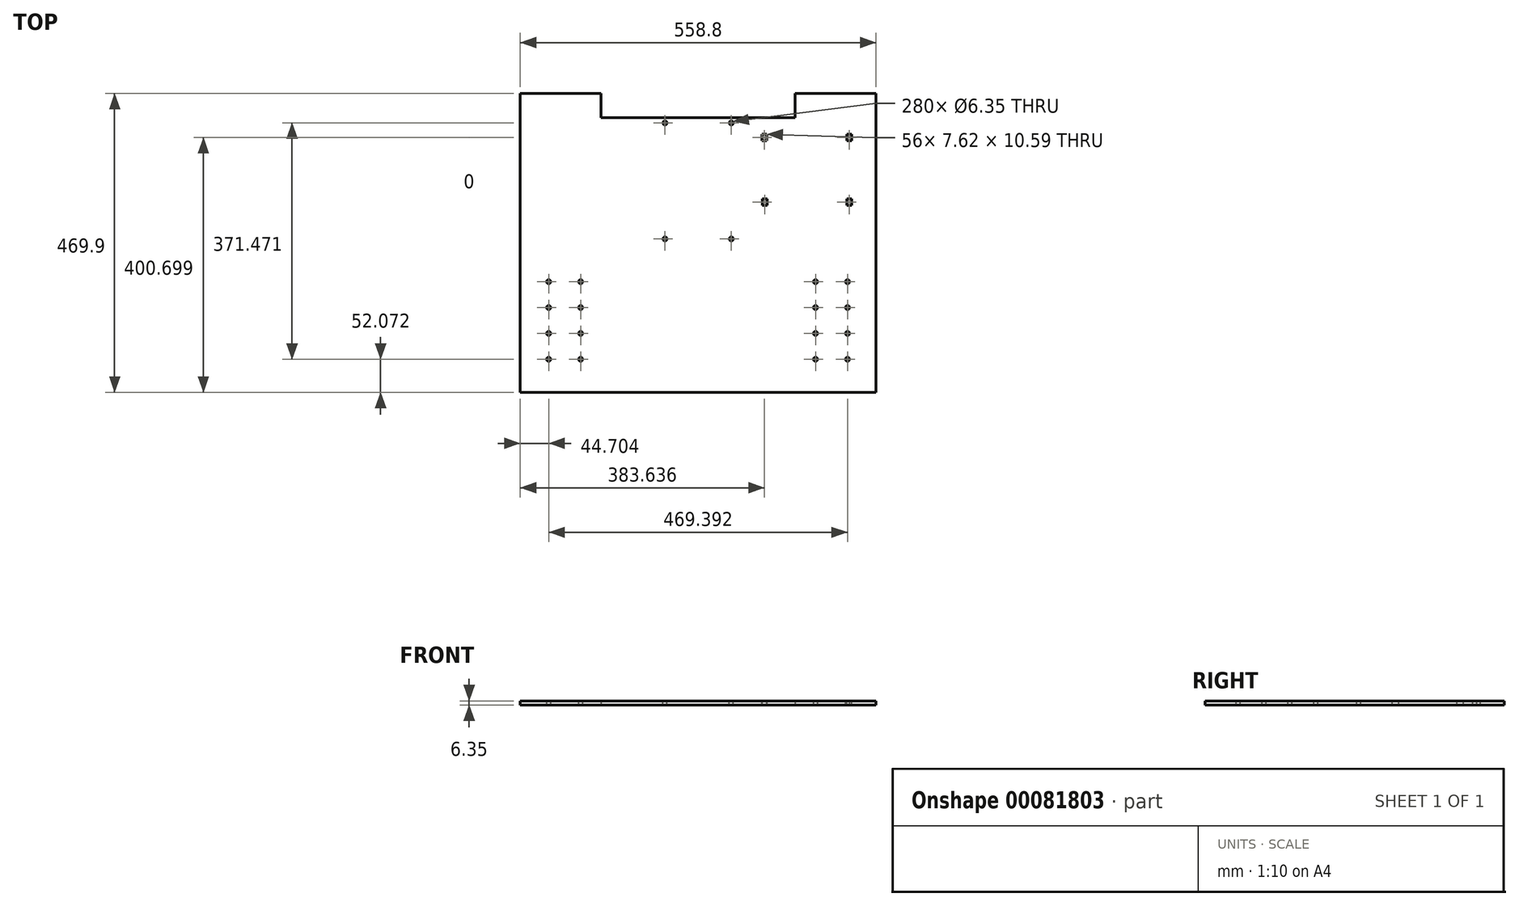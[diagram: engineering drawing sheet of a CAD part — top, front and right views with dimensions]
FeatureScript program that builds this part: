
annotation { "Feature Type Name" : "Feature", "Feature Type Description" : "" }
export const myFeature = defineFeature(function(context is Context, id is Id, definition is map)
    precondition{}
    {
        {
            var Q0;
            Q0=qCreatedBy(makeId("Top.planeOp"),FACE);
            var sketch = newSketch(context, id + "F0", { "sketchPlane" : qUnion([Q0])});
            skLineSegment(sketch, "E0.top", {"start": v(-279.4, -241.27) * mm, "end": v(279.4, -241.27) * mm});
            skLineSegment(sketch, "E0.left", {"start": v(-279.4, 228.63) * mm, "end": v(-279.4, -241.27) * mm});
            skLineSegment(sketch, "E0.right", {"start": v(279.4, 228.63) * mm, "end": v(279.4, -241.27) * mm});
            skLineSegment(sketch, "E1.top", {"start": v(-152.4, 190.53) * mm, "end": v(152.4, 190.53) * mm});
            skLineSegment(sketch, "E1.left", {"start": v(-152.4, 228.63) * mm, "end": v(-152.4, 190.53) * mm});
            skLineSegment(sketch, "E1.right", {"start": v(152.4, 228.63) * mm, "end": v(152.4, 190.53) * mm});
            skLineSegment(sketch, "E2", {"start": v(-279.4, 228.63) * mm, "end": v(-152.4, 228.63) * mm});
            skLineSegment(sketch, "E3", {"start": v(152.4, 228.63) * mm, "end": v(279.4, 228.63) * mm});
            skSolve(sketch);
        }
        {
            var Q0;
            Q0=makeQuery(id+"F0.imprint","IMPRINT",FACE,{"disambiguationData":[TD([[makeQuery(id+"F0.imprint","IMPRINT",EDGE,{"derivedFrom":sQuery(id+"F0.wireOp",EDGE,"E0.top")}),1.0]])]});
            extrude(context, id + "F1", {"entities" : qUnion([Q0]), "depth" : 6.35 * mm});
        }
        {
            var Q0;
            Q0=makeQuery(id+"F1.opExtrude","CAP_FACE",FACE,{"disambiguationData":[OSD([sQuery(id+"F0.wireOp",EDGE,"E0.top"),sQuery(id+"F0.wireOp",EDGE,"E0.left"),sQuery(id+"F0.wireOp",EDGE,"E0.right"),sQuery(id+"F0.wireOp",EDGE,"E1.top"),sQuery(id+"F0.wireOp",EDGE,"E1.left"),sQuery(id+"F0.wireOp",EDGE,"E1.right"),sQuery(id+"F0.wireOp",EDGE,"E2"),sQuery(id+"F0.wireOp",EDGE,"E3")])],"isStart":false});
            var sketch = newSketch(context, id + "F2", { "sketchPlane" : qUnion([Q0])});
            skLineSegment(sketch, "E4.bottom", {"start": v(-241.3, -203.17) * mm, "end": v(-177.8, -203.17) * mm});
            skLineSegment(sketch, "E4.top", {"start": v(-241.3, -175.23) * mm, "end": v(-177.8, -175.23) * mm});
            skLineSegment(sketch, "E4.left", {"start": v(-241.3, -203.17) * mm, "end": v(-241.3, -175.23) * mm});
            skLineSegment(sketch, "E4.right", {"start": v(-177.8, -203.17) * mm, "end": v(-177.8, -175.23) * mm});
            skCircle(sketch, "E5", {"center": v(-234.69, -189.2) * mm, "radius": 2.2 * mm});
            skCircle(sketch, "E6", {"center": v(-184.42, -189.2) * mm, "radius": 2.2 * mm});
            skSolve(sketch);
        }
        {
            var Q0;
            Q0=sQuery(id+"F2.wireOp",VERTEX,"E5.center");
            var Q1;
            Q1=sQuery(id+"F2.wireOp",VERTEX,"E6.center");
            var Q2;
            Q2=makeQuery(id+"F1.opExtrude","SWEPT_BODY",BODY,{"disambiguationData":[OSD([sQuery(id+"F0.wireOp",EDGE,"E0.top"),sQuery(id+"F0.wireOp",EDGE,"E0.left"),sQuery(id+"F0.wireOp",EDGE,"E0.right"),sQuery(id+"F0.wireOp",EDGE,"E1.top"),sQuery(id+"F0.wireOp",EDGE,"E1.left"),sQuery(id+"F0.wireOp",EDGE,"E1.right"),sQuery(id+"F0.wireOp",EDGE,"E2"),sQuery(id+"F0.wireOp",EDGE,"E3")])]});
            hole(context, id + "F3", {"style" : HoleStyle.SIMPLE, "endStyle" : HoleEndStyle.THROUGH, "holeDiameter" : 6.35 * mm, "locations" : qUnion([Q0, Q1]), "scope" : qUnion([Q2]), "isTappedThrough" : true});
        }
        {
            var Q0;
            Q0=makeQuery(id+"F2.imprint","IMPRINT",FACE,{"disambiguationData":[TD([[makeQuery(id+"F2.imprint","IMPRINT",EDGE,{"derivedFrom":sQuery(id+"F2.wireOp",EDGE,"E4.bottom")}),-1.0]])]});
            var sketch = newSketch(context, id + "F4", { "sketchPlane" : qUnion([Q0])});
            skCircle(sketch, "E7", {"center": v(-234.7, -148.56) * mm, "radius": 3.18 * mm});
            skCircle(sketch, "E8", {"center": v(-234.7, -107.92) * mm, "radius": 3.18 * mm});
            skCircle(sketch, "E9", {"center": v(-234.7, -67.28) * mm, "radius": 3.18 * mm});
            skLineSegment(sketch, "E10", {"start": v(-241.3, -175.23) * mm, "end": v(-98.93, -175.23) * mm});
            skCircle(sketch, "E11", {"center": v(-184.43, -67.28) * mm, "radius": 3.18 * mm});
            skCircle(sketch, "E12", {"center": v(-184.43, -107.92) * mm, "radius": 3.18 * mm});
            skCircle(sketch, "E13", {"center": v(-184.43, -148.56) * mm, "radius": 3.18 * mm});
            skSolve(sketch);
        }
        {
            var Q0;
            Q0=sQuery(id+"F4.wireOp",VERTEX,"E9.center");
            var Q1;
            Q1=sQuery(id+"F4.wireOp",VERTEX,"E11.center");
            var Q2;
            Q2=sQuery(id+"F4.wireOp",VERTEX,"E12.center");
            var Q3;
            Q3=sQuery(id+"F4.wireOp",VERTEX,"E8.center");
            var Q4;
            Q4=sQuery(id+"F4.wireOp",VERTEX,"E7.center");
            var Q5;
            Q5=sQuery(id+"F4.wireOp",VERTEX,"E13.center");
            var Q6;
            Q6=makeQuery(id+"F1.opExtrude","SWEPT_BODY",BODY,{"disambiguationData":[OSD([sQuery(id+"F0.wireOp",EDGE,"E0.top"),sQuery(id+"F0.wireOp",EDGE,"E0.left"),sQuery(id+"F0.wireOp",EDGE,"E0.right"),sQuery(id+"F0.wireOp",EDGE,"E1.top"),sQuery(id+"F0.wireOp",EDGE,"E1.left"),sQuery(id+"F0.wireOp",EDGE,"E1.right"),sQuery(id+"F0.wireOp",EDGE,"E2"),sQuery(id+"F0.wireOp",EDGE,"E3")])]});
            hole(context, id + "F5", {"style" : HoleStyle.SIMPLE, "endStyle" : HoleEndStyle.THROUGH, "holeDiameter" : 6.35 * mm, "locations" : qUnion([Q0, Q1, Q2, Q3, Q4, Q5]), "scope" : qUnion([Q6]), "isTappedThrough" : true});
        }
        {
            var Q0;
            Q0=makeQuery(id+"F2.imprint","IMPRINT",FACE,{"disambiguationData":[TD([[makeQuery(id+"F2.imprint","IMPRINT",EDGE,{"derivedFrom":sQuery(id+"F2.wireOp",EDGE,"E4.bottom")}),-1.0]])]});
            var sketch = newSketch(context, id + "F6", { "sketchPlane" : qUnion([Q0])});
            skLineSegment(sketch, "E14.bottom", {"start": v(177.8, -203.17) * mm, "end": v(241.3, -203.17) * mm});
            skLineSegment(sketch, "E14.top", {"start": v(177.8, -175.23) * mm, "end": v(241.3, -175.23) * mm});
            skLineSegment(sketch, "E14.left", {"start": v(177.8, -203.17) * mm, "end": v(177.8, -175.23) * mm});
            skLineSegment(sketch, "E14.right", {"start": v(241.3, -203.17) * mm, "end": v(241.3, -175.23) * mm});
            skCircle(sketch, "E15", {"center": v(184.4, -189.2) * mm, "radius": 3.18 * mm});
            skCircle(sketch, "E16", {"center": v(234.67, -189.2) * mm, "radius": 3.18 * mm});
            skSolve(sketch);
        }
        {
            var Q0;
            Q0=makeQuery(id+"F2.imprint","IMPRINT",FACE,{"disambiguationData":[TD([[makeQuery(id+"F2.imprint","IMPRINT",EDGE,{"derivedFrom":sQuery(id+"F2.wireOp",EDGE,"E4.bottom")}),-1.0]])]});
            var sketch = newSketch(context, id + "F7", { "sketchPlane" : qUnion([Q0])});
            skCircle(sketch, "E17", {"center": v(184.43, -148.56) * mm, "radius": 3.18 * mm});
            skCircle(sketch, "E18", {"center": v(234.7, -148.56) * mm, "radius": 3.18 * mm});
            skLineSegment(sketch, "E19", {"start": v(241.7, -175.23) * mm, "end": v(151.62, -175.23) * mm});
            skCircle(sketch, "E20", {"center": v(234.7, -107.92) * mm, "radius": 3.17 * mm});
            skCircle(sketch, "E21", {"center": v(184.43, -107.92) * mm, "radius": 3.18 * mm});
            skCircle(sketch, "E22", {"center": v(184.43, -67.28) * mm, "radius": 3.18 * mm});
            skCircle(sketch, "E23", {"center": v(234.7, -67.28) * mm, "radius": 3.18 * mm});
            skSolve(sketch);
        }
        {
            var Q0;
            Q0=sQuery(id+"F6.wireOp",VERTEX,"E15.center");
            var Q1;
            Q1=sQuery(id+"F6.wireOp",VERTEX,"E16.center");
            var Q2;
            Q2=sQuery(id+"F7.wireOp",VERTEX,"E18.center");
            var Q3;
            Q3=sQuery(id+"F7.wireOp",VERTEX,"E17.center");
            var Q4;
            Q4=sQuery(id+"F7.wireOp",VERTEX,"E21.center");
            var Q5;
            Q5=sQuery(id+"F7.wireOp",VERTEX,"E20.center");
            var Q6;
            Q6=sQuery(id+"F7.wireOp",VERTEX,"E23.center");
            var Q7;
            Q7=sQuery(id+"F7.wireOp",VERTEX,"E22.center");
            var Q8;
            Q8=makeQuery(id+"F1.opExtrude","SWEPT_BODY",BODY,{"disambiguationData":[OSD([sQuery(id+"F0.wireOp",EDGE,"E0.top"),sQuery(id+"F0.wireOp",EDGE,"E0.left"),sQuery(id+"F0.wireOp",EDGE,"E0.right"),sQuery(id+"F0.wireOp",EDGE,"E1.top"),sQuery(id+"F0.wireOp",EDGE,"E1.left"),sQuery(id+"F0.wireOp",EDGE,"E1.right"),sQuery(id+"F0.wireOp",EDGE,"E2"),sQuery(id+"F0.wireOp",EDGE,"E3")])]});
            hole(context, id + "F8", {"style" : HoleStyle.SIMPLE, "endStyle" : HoleEndStyle.THROUGH, "holeDiameter" : 6.35 * mm, "locations" : qUnion([Q0, Q1, Q2, Q3, Q4, Q5, Q6, Q7]), "scope" : qUnion([Q8]), "isTappedThrough" : true});
        }
        {
            var Q0;
            Q0=makeQuery(id+"F2.imprint","IMPRINT",FACE,{"disambiguationData":[TD([[makeQuery(id+"F2.imprint","IMPRINT",EDGE,{"derivedFrom":sQuery(id+"F2.wireOp",EDGE,"E4.bottom")}),-1.0]])]});
            var sketch = newSketch(context, id + "F9", { "sketchPlane" : qUnion([Q0])});
            skLineSegment(sketch, "E24.top", {"start": v(-57.15, -14.11) * mm, "end": v(57.15, -14.11) * mm});
            skLineSegment(sketch, "E24.left", {"start": v(-57.15, 177.83) * mm, "end": v(-57.15, -14.11) * mm});
            skLineSegment(sketch, "E24.right", {"start": v(57.15, 177.83) * mm, "end": v(57.15, -14.11) * mm});
            skCircle(sketch, "E25", {"center": v(-52.07, 182.27) * mm, "radius": 2.67 * mm});
            skCircle(sketch, "E26", {"center": v(52.07, 182.27) * mm, "radius": 2.67 * mm});
            skCircle(sketch, "E27", {"center": v(-52.07, 0) * mm, "radius": 2.67 * mm});
            skCircle(sketch, "E28", {"center": v(52.07, 0) * mm, "radius": 2.67 * mm});
            skSolve(sketch);
        }
        {
            var Q0;
            Q0=sQuery(id+"F9.wireOp",VERTEX,"E25.center");
            var Q1;
            Q1=sQuery(id+"F9.wireOp",VERTEX,"E26.center");
            var Q2;
            Q2=sQuery(id+"F9.wireOp",VERTEX,"E28.center");
            var Q3;
            Q3=sQuery(id+"F9.wireOp",VERTEX,"E27.center");
            var Q4;
            Q4=makeQuery(id+"F1.opExtrude","SWEPT_BODY",BODY,{"disambiguationData":[OSD([sQuery(id+"F0.wireOp",EDGE,"E0.top"),sQuery(id+"F0.wireOp",EDGE,"E0.left"),sQuery(id+"F0.wireOp",EDGE,"E0.right"),sQuery(id+"F0.wireOp",EDGE,"E1.top"),sQuery(id+"F0.wireOp",EDGE,"E1.left"),sQuery(id+"F0.wireOp",EDGE,"E1.right"),sQuery(id+"F0.wireOp",EDGE,"E2"),sQuery(id+"F0.wireOp",EDGE,"E3")])]});
            hole(context, id + "F10", {"style" : HoleStyle.SIMPLE, "endStyle" : HoleEndStyle.THROUGH, "holeDiameter" : 6.35 * mm, "locations" : qUnion([Q0, Q1, Q2, Q3]), "scope" : qUnion([Q4]), "isTappedThrough" : true});
        }
        {
            var Q0;
            Q0=makeQuery(id+"F2.imprint","IMPRINT",FACE,{"disambiguationData":[TD([[makeQuery(id+"F2.imprint","IMPRINT",EDGE,{"derivedFrom":sQuery(id+"F2.wireOp",EDGE,"E4.bottom")}),-1.0]])]});
            var sketch = newSketch(context, id + "F11", { "sketchPlane" : qUnion([Q0])});
            skLineSegment(sketch, "E29.bottom", {"start": v(100.36, 177.83) * mm, "end": v(241.3, 177.83) * mm});
            skLineSegment(sketch, "E29.top", {"start": v(100.36, 39.43) * mm, "end": v(241.3, 39.43) * mm});
            skLineSegment(sketch, "E29.left", {"start": v(100.36, 177.83) * mm, "end": v(100.36, 39.43) * mm});
            skLineSegment(sketch, "E29.right", {"start": v(241.3, 177.83) * mm, "end": v(241.3, 39.43) * mm});
            skLineSegment(sketch, "E30.bottom", {"start": v(233.4, 63.13) * mm, "end": v(241.02, 63.13) * mm});
            skLineSegment(sketch, "E30.top", {"start": v(233.4, 52.53) * mm, "end": v(241.02, 52.53) * mm});
            skLineSegment(sketch, "E30.left", {"start": v(233.4, 63.13) * mm, "end": v(233.4, 52.53) * mm});
            skLineSegment(sketch, "E30.right", {"start": v(241.02, 63.13) * mm, "end": v(241.02, 52.53) * mm});
            skLineSegment(sketch, "E31.bottom", {"start": v(233.6, 164.73) * mm, "end": v(241.23, 164.73) * mm});
            skLineSegment(sketch, "E31.top", {"start": v(233.6, 154.13) * mm, "end": v(241.23, 154.13) * mm});
            skLineSegment(sketch, "E31.left", {"start": v(233.6, 164.73) * mm, "end": v(233.6, 154.13) * mm});
            skLineSegment(sketch, "E31.right", {"start": v(241.23, 164.73) * mm, "end": v(241.23, 154.13) * mm});
            skLineSegment(sketch, "E32.bottom", {"start": v(108.05, 164.73) * mm, "end": v(100.43, 164.73) * mm});
            skLineSegment(sketch, "E32.top", {"start": v(108.05, 154.13) * mm, "end": v(100.43, 154.13) * mm});
            skLineSegment(sketch, "E32.left", {"start": v(108.05, 164.73) * mm, "end": v(108.05, 154.13) * mm});
            skLineSegment(sketch, "E32.right", {"start": v(100.43, 164.73) * mm, "end": v(100.43, 154.13) * mm});
            skLineSegment(sketch, "E33.bottom", {"start": v(108.25, 63.13) * mm, "end": v(100.63, 63.13) * mm});
            skLineSegment(sketch, "E33.top", {"start": v(108.25, 52.53) * mm, "end": v(100.63, 52.53) * mm});
            skLineSegment(sketch, "E33.left", {"start": v(108.25, 63.13) * mm, "end": v(108.25, 52.53) * mm});
            skLineSegment(sketch, "E33.right", {"start": v(100.63, 63.13) * mm, "end": v(100.63, 52.53) * mm});
            skSolve(sketch);
        }
        {
            var Q0;
            Q0=makeQuery(id+"F11.imprint","IMPRINT",FACE,{"disambiguationData":[TD([[makeQuery(id+"F11.imprint","IMPRINT",EDGE,{"derivedFrom":sQuery(id+"F11.wireOp",EDGE,"E33.bottom")}),1.0]])]});
            var Q1;
            Q1=makeQuery(id+"F11.imprint","IMPRINT",FACE,{"disambiguationData":[TD([[makeQuery(id+"F11.imprint","IMPRINT",EDGE,{"derivedFrom":sQuery(id+"F11.wireOp",EDGE,"E32.bottom")}),1.0]])]});
            var Q2;
            Q2=makeQuery(id+"F11.imprint","IMPRINT",FACE,{"disambiguationData":[TD([[makeQuery(id+"F11.imprint","IMPRINT",EDGE,{"derivedFrom":sQuery(id+"F11.wireOp",EDGE,"E31.bottom")}),-1.0]])]});
            var Q3;
            Q3=makeQuery(id+"F11.imprint","IMPRINT",FACE,{"disambiguationData":[TD([[makeQuery(id+"F11.imprint","IMPRINT",EDGE,{"derivedFrom":sQuery(id+"F11.wireOp",EDGE,"E30.bottom")}),-1.0]])]});
            extrude(context, id + "F12", {"entities" : qUnion([Q0, Q1, Q2, Q3]), "operationType" : NewBodyOperationType.REMOVE, "oppositeDirection" : true, "depth" : 25.4 * mm});
        }
    });
